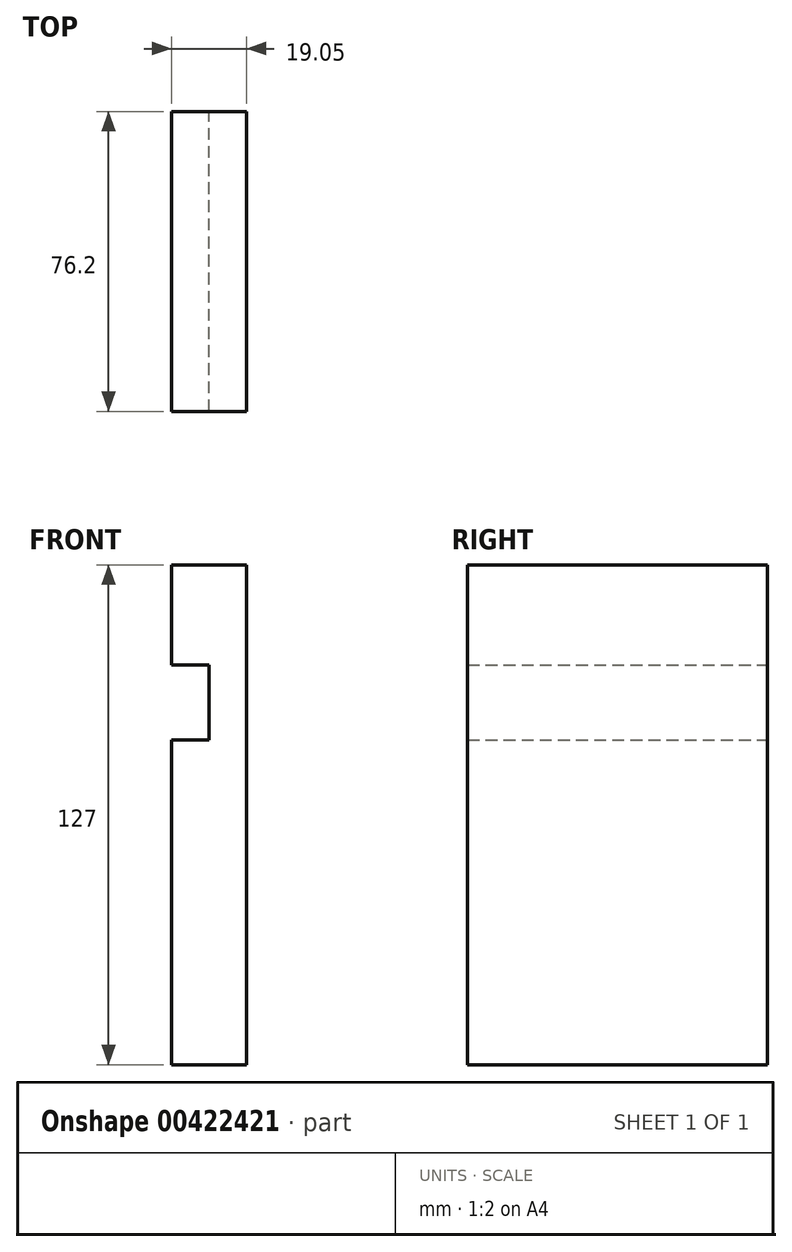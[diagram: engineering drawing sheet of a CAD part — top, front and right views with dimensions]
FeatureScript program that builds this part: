
annotation { "Feature Type Name" : "Feature", "Feature Type Description" : "" }
export const myFeature = defineFeature(function(context is Context, id is Id, definition is map)
    precondition{}
    {
        {
            var Q0;
            Q0=qCreatedBy(makeId("Front.planeOp"),FACE);
            var sketch = newSketch(context, id + "F0", { "sketchPlane" : qUnion([Q0])});
            skLineSegment(sketch, "E0", {"start": v(0, 59.97) * mm, "end": v(0, -67.03) * mm});
            skLineSegment(sketch, "E1", {"start": v(0, -67.03) * mm, "end": v(-19.05, -67.03) * mm});
            skLineSegment(sketch, "E2", {"start": v(0, 59.97) * mm, "end": v(-19.05, 59.97) * mm});
            skLineSegment(sketch, "E3", {"start": v(-19.05, 59.97) * mm, "end": v(-19.05, 34.57) * mm});
            skLineSegment(sketch, "E4", {"start": v(-19.05, 34.57) * mm, "end": v(-9.52, 34.57) * mm});
            skLineSegment(sketch, "E5", {"start": v(-9.52, 34.57) * mm, "end": v(-9.52, 15.52) * mm});
            skLineSegment(sketch, "E6", {"start": v(-9.52, 15.52) * mm, "end": v(-19.05, 15.52) * mm});
            skLineSegment(sketch, "E7", {"start": v(-19.05, 15.52) * mm, "end": v(-19.05, -67.03) * mm});
            skSolve(sketch);
        }
        {
            var Q0;
            Q0 = qSketchRegion(id + "F0", true);
            extrude(context, id + "F1", {"entities" : qUnion([Q0]), "depth" : 76.2 * mm});
        }
    });
